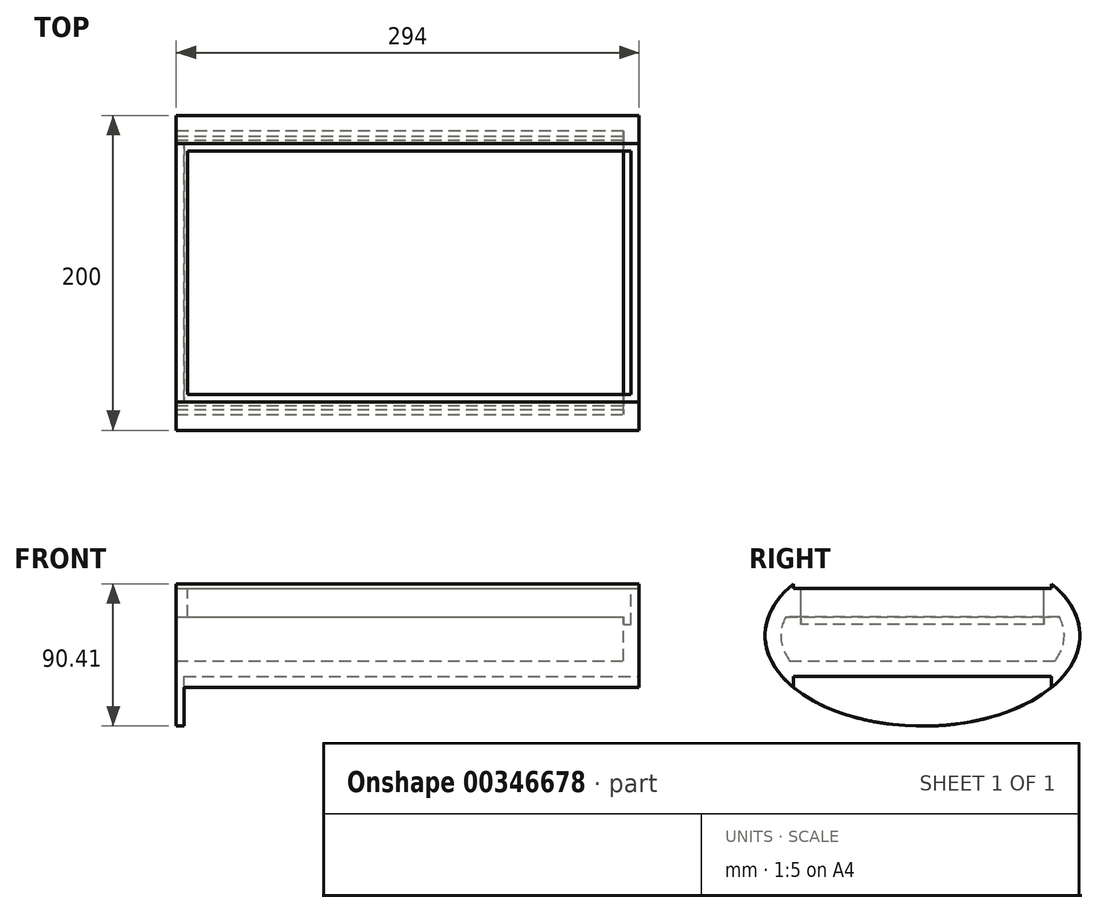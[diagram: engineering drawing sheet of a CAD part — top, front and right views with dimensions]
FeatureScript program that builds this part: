
annotation { "Feature Type Name" : "Feature", "Feature Type Description" : "" }
export const myFeature = defineFeature(function(context is Context, id is Id, definition is map)
    precondition{}
    {
        {
            var Q0;
            Q0=qCreatedBy(makeId("Top.planeOp"),FACE);
            var sketch = newSketch(context, id + "F0", { "sketchPlane" : qUnion([Q0])});
            skLineSegment(sketch, "E0.bottom", {"start": v(-139.7, 76.2) * mm, "end": v(139.7, 76.2) * mm});
            skLineSegment(sketch, "E0.top", {"start": v(-139.7, -76.2) * mm, "end": v(139.7, -76.2) * mm});
            skLineSegment(sketch, "E0.left", {"start": v(-139.7, 76.2) * mm, "end": v(-139.7, -76.2) * mm});
            skLineSegment(sketch, "E0.right", {"start": v(139.7, 76.2) * mm, "end": v(139.7, -76.2) * mm});
            skCircle(sketch, "E1", {"center": v(-9.53, 69.85) * mm, "radius": 3.1 * mm});
            skCircle(sketch, "E2", {"center": v(-6.2, -69.85) * mm, "radius": 3.1 * mm});
            skCircle(sketch, "E3", {"center": v(133.35, -69.85) * mm, "radius": 3.1 * mm});
            skCircle(sketch, "E4", {"center": v(133.35, 0) * mm, "radius": 3.1 * mm});
            skCircle(sketch, "E5", {"center": v(63.5, 0) * mm, "radius": 3.1 * mm});
            skCircle(sketch, "E6", {"center": v(133.35, 69.85) * mm, "radius": 3.1 * mm});
            skPoint(sketch, "E7", {"position": v(0, -76.2) * mm});
            skCircle(sketch, "E8.MirrorC", {"center": v(-133.35, 69.85) * mm, "radius": 3.1 * mm});
            skCircle(sketch, "E9.MirrorC", {"center": v(-133.35, 0) * mm, "radius": 3.1 * mm});
            skCircle(sketch, "E10.MirrorC", {"center": v(-133.35, -69.85) * mm, "radius": 3.1 * mm});
            skCircle(sketch, "E11.MirrorC", {"center": v(-63.5, 0) * mm, "radius": 3.1 * mm});
            skSolve(sketch);
        }
        {
            var Q0;
            Q0=qSketchRegion(id+"F0",true);
            extrude(context, id + "F1", {"entities" : qUnion([Q0]), "depth" : 2 * mm});
        }
        {
            var Q0;
            Q0=makeQuery(id+"F1.opExtrude","CAP_FACE",FACE,{"disambiguationData":[OSD([sQuery(id+"F0.wireOp",EDGE,"E0.bottom"),sQuery(id+"F0.wireOp",EDGE,"E0.top"),sQuery(id+"F0.wireOp",EDGE,"E0.left"),sQuery(id+"F0.wireOp",EDGE,"E0.right"),sQuery(id+"F0.wireOp",EDGE,"E1"),sQuery(id+"F0.wireOp",EDGE,"E2"),sQuery(id+"F0.wireOp",EDGE,"E3"),sQuery(id+"F0.wireOp",EDGE,"E4"),sQuery(id+"F0.wireOp",EDGE,"E5"),sQuery(id+"F0.wireOp",EDGE,"E6"),sQuery(id+"F0.wireOp",EDGE,"E8.MirrorC"),sQuery(id+"F0.wireOp",EDGE,"E9.MirrorC"),sQuery(id+"F0.wireOp",EDGE,"E10.MirrorC"),sQuery(id+"F0.wireOp",EDGE,"E11.MirrorC")])],"isStart":false});
            var sketch = newSketch(context, id + "F2", { "sketchPlane" : qUnion([Q0])});
            skCircle(sketch, "E12", {"center": v(38.1, 25.4) * mm, "radius": 12.7 * mm});
            skCircle(sketch, "E13", {"center": v(88.9, 25.4) * mm, "radius": 12.7 * mm});
            skCircle(sketch, "E14", {"center": v(88.9, -25.4) * mm, "radius": 12.7 * mm});
            skCircle(sketch, "E15", {"center": v(38.1, -25.4) * mm, "radius": 12.7 * mm});
            skCircle(sketch, "E16.MirrorC", {"center": v(-38.1, 25.4) * mm, "radius": 12.7 * mm});
            skCircle(sketch, "E17.MirrorC", {"center": v(-88.9, 25.4) * mm, "radius": 12.7 * mm});
            skCircle(sketch, "E18.MirrorC", {"center": v(-88.9, -25.4) * mm, "radius": 12.7 * mm});
            skCircle(sketch, "E19.MirrorC", {"center": v(-38.1, -25.4) * mm, "radius": 12.7 * mm});
            skSolve(sketch);
        }
        {
            var Q0;
            Q0=makeQuery(id+"F2.imprint","IMPRINT",FACE,{"disambiguationData":[TD([[makeQuery(id+"F2.imprint","IMPRINT",EDGE,{"derivedFrom":sQuery(id+"F2.wireOp",EDGE,"E12")}),-1.0]])]});
            extrude(context, id + "F3", {"entities" : qUnion([Q0]), "operationType" : NewBodyOperationType.REMOVE, "oppositeDirection" : true, "depth" : .1 * mm});
        }
        {
            var Q0;
            Q0=makeQuery(id+"F1.opExtrude","CAP_FACE",FACE,{"disambiguationData":[OSD([sQuery(id+"F0.wireOp",EDGE,"E0.bottom"),sQuery(id+"F0.wireOp",EDGE,"E0.top"),sQuery(id+"F0.wireOp",EDGE,"E0.left"),sQuery(id+"F0.wireOp",EDGE,"E0.right"),sQuery(id+"F0.wireOp",EDGE,"E1"),sQuery(id+"F0.wireOp",EDGE,"E2"),sQuery(id+"F0.wireOp",EDGE,"E3"),sQuery(id+"F0.wireOp",EDGE,"E4"),sQuery(id+"F0.wireOp",EDGE,"E5"),sQuery(id+"F0.wireOp",EDGE,"E6"),sQuery(id+"F0.wireOp",EDGE,"E8.MirrorC"),sQuery(id+"F0.wireOp",EDGE,"E9.MirrorC"),sQuery(id+"F0.wireOp",EDGE,"E10.MirrorC"),sQuery(id+"F0.wireOp",EDGE,"E11.MirrorC")])],"isStart":true});
            var sketch = newSketch(context, id + "F4", { "sketchPlane" : qUnion([Q0])});
            skCircle(sketch, "E20", {"center": v(88.9, 61.12) * mm, "radius": 9.52 * mm});
            skCircle(sketch, "E21", {"center": v(-72.61, 61.12) * mm, "radius": 9.52 * mm});
            skCircle(sketch, "E22", {"center": v(-72.61, -60.83) * mm, "radius": 9.52 * mm});
            skCircle(sketch, "E23", {"center": v(88.9, -60.83) * mm, "radius": 9.52 * mm});
            skSolve(sketch);
        }
        {
            var Q0;
            Q0=qSketchRegion(id+"F4",true);
            extrude(context, id + "F5", {"entities" : qUnion([Q0]), "operationType" : NewBodyOperationType.REMOVE, "oppositeDirection" : true, "depth" : .1 * mm});
        }
        {
            var Q0;
            Q0=qCreatedBy(makeId("Right.planeOp"),FACE);
            cPlane(context, id + "F6", {"entities" : qUnion([Q0]), "cplaneType" : CPlaneType.OFFSET, "offset" : 148 * mm, "oppositeDirection" : true, "width" : 150 * mm, "height" : 150 * mm});
        }
        {
            var Q0;
            Q0=qCreatedBy(makeId("Right.planeOp"),FACE);
            cPlane(context, id + "F7", {"entities" : qUnion([Q0]), "cplaneType" : CPlaneType.OFFSET, "offset" : 146 * mm, "width" : 150 * mm, "height" : 150 * mm});
        }
        {
            var Q0;
            Q0=qCreatedBy(makeId("Top.planeOp"),FACE);
            cPlane(context, id + "F8", {"entities" : qUnion([Q0]), "cplaneType" : CPlaneType.OFFSET, "offset" : 51 * mm, "oppositeDirection" : true, "width" : 150 * mm, "height" : 150 * mm});
        }
        {
            var Q0;
            Q0=qCreatedBy(id+"F6.planeOp",FACE);
            var sketch = newSketch(context, id + "F9", { "sketchPlane" : qUnion([Q0])});
            skEllipse(sketch, "E24", {"center": v(0, -30) * mm, "majorRadius": 100 * mm, "minorRadius": 57.5 * mm, "majorAxis": v(-1, 0)});
            skSolve(sketch);
        }
        {
            var Q0;
            Q0=qCreatedBy(id+"F7.planeOp",FACE);
            var sketch = newSketch(context, id + "F10", { "sketchPlane" : qUnion([Q0])});
            skEllipse(sketch, "E25", {"center": v(0, -30) * mm, "majorRadius": 100 * mm, "minorRadius": 57.5 * mm, "majorAxis": v(1, 0)});
            skSolve(sketch);
        }
        {
            var Q1;
            Q1=makeQuery(id+"F9.imprint","IMPRINT",FACE,{"disambiguationData":[TD([[makeQuery(id+"F9.imprint","IMPRINT",EDGE,{"derivedFrom":sQuery(id+"F9.wireOp",EDGE,"E24")}),1.0]])]});
            var Q2;
            Q2=makeQuery(id+"F10.imprint","IMPRINT",FACE,{"disambiguationData":[TD([[makeQuery(id+"F10.imprint","IMPRINT",EDGE,{"derivedFrom":sQuery(id+"F10.wireOp",EDGE,"E25")}),1.0]])]});
            loft(context, id + "F11", {"sheetProfilesArray" : [{ "sheetProfileEntities" : qUnion([Q1]) }, { "sheetProfileEntities" : qUnion([Q2]) }]});
        }
        {
            var Q0;
            Q0=qCreatedBy(id+"F8.planeOp",FACE);
            cPlane(context, id + "F12", {"entities" : qUnion([Q0]), "cplaneType" : CPlaneType.OFFSET, "offset" : 5 * mm, "oppositeDirection" : true, "width" : 150 * mm, "height" : 150 * mm});
        }
        {
            var Q0;
            Q0=qCreatedBy(id+"F12.planeOp",FACE);
            var sketch = newSketch(context, id + "F13", { "sketchPlane" : qUnion([Q0])});
            skLineSegment(sketch, "E26.bottom", {"start": v(-143, -82) * mm, "end": v(146, -82) * mm});
            skLineSegment(sketch, "E26.top", {"start": v(-143, 82) * mm, "end": v(146, 82) * mm});
            skLineSegment(sketch, "E26.left", {"start": v(-143, -82) * mm, "end": v(-143, 82) * mm});
            skLineSegment(sketch, "E26.right", {"start": v(146, -82) * mm, "end": v(146, 82) * mm});
            skSolve(sketch);
        }
        {
            var Q0;
            Q0=qCreatedBy(makeId("Top.planeOp"),FACE);
            var sketch = newSketch(context, id + "F14", { "sketchPlane" : qUnion([Q0])});
            skLineSegment(sketch, "E27.bottom", {"start": v(-148, 82) * mm, "end": v(146, 82) * mm});
            skLineSegment(sketch, "E27.top", {"start": v(-148, -82) * mm, "end": v(146, -82) * mm});
            skLineSegment(sketch, "E27.left", {"start": v(-148, 82) * mm, "end": v(-148, -82) * mm});
            skLineSegment(sketch, "E27.right", {"start": v(146, 82) * mm, "end": v(146, -82) * mm});
            skSolve(sketch);
        }
        {
            var Q0;
            Q0=qSketchRegion(id+"F14",true);
            extrude(context, id + "F15", {"entities" : qUnion([Q0]), "operationType" : NewBodyOperationType.REMOVE, "depth" : 32 * mm});
        }
        {
            var Q0;
            Q0=makeQuery(id+"F13.imprint","IMPRINT",FACE,{"disambiguationData":[TD([[makeQuery(id+"F13.imprint","IMPRINT",EDGE,{"derivedFrom":sQuery(id+"F13.wireOp",EDGE,"E26.bottom")}),1.0]])]});
            extrude(context, id + "F16", {"entities" : qUnion([Q0]), "operationType" : NewBodyOperationType.REMOVE, "oppositeDirection" : true, "depth" : 40 * mm});
        }
        {
            var Q0;
            Q0=makeQuery(id+"F2.imprint","IMPRINT",FACE,{"disambiguationData":[TD([[makeQuery(id+"F2.imprint","IMPRINT",EDGE,{"derivedFrom":sQuery(id+"F2.wireOp",EDGE,"E12")}),-1.0]])]});
            var sketch = newSketch(context, id + "F17", { "sketchPlane" : qUnion([Q0])});
            skLineSegment(sketch, "E28.bottom", {"start": v(-140.7, 77.2) * mm, "end": v(140.7, 77.2) * mm});
            skLineSegment(sketch, "E28.top", {"start": v(-140.7, -77.2) * mm, "end": v(140.7, -77.2) * mm});
            skLineSegment(sketch, "E28.left", {"start": v(-140.7, 77.2) * mm, "end": v(-140.7, -77.2) * mm});
            skLineSegment(sketch, "E28.right", {"start": v(140.7, 77.2) * mm, "end": v(140.7, -77.2) * mm});
            skSolve(sketch);
        }
        {
            var Q0;
            Q0=qSketchRegion(id+"F17",true);
            extrude(context, id + "F18", {"entities" : qUnion([Q0]), "operationType" : NewBodyOperationType.REMOVE, "oppositeDirection" : true, "depth" : 10 * mm});
        }
        {
            var Q0;
            Q0=makeQuery(id+"F11.opLoft","CAP_FACE",FACE,{"disambiguationData":[OSD([makeQuery(id+"F9.imprint","IMPRINT",FACE,{"disambiguationData":[TD([[makeQuery(id+"F9.imprint","IMPRINT",EDGE,{"derivedFrom":sQuery(id+"F9.wireOp",EDGE,"E24")}),1.0]])]})])],"isStart":true});
            var Q1;
            Q1=makeQuery(id+"F11.opLoft","CAP_FACE",FACE,{"disambiguationData":[OSD([makeQuery(id+"F10.imprint","IMPRINT",FACE,{"disambiguationData":[TD([[makeQuery(id+"F10.imprint","IMPRINT",EDGE,{"derivedFrom":sQuery(id+"F10.wireOp",EDGE,"E25")}),1.0]])]})])],"isStart":true});
            shell(context, id + "F19", {"entities" : qUnion([Q0, Q1]), "thickness" : 10 * mm});
        }
        {
            var Q0;
            Q0=qSketchRegion(id+"F17",true);
            extrude(context, id + "F20", {"entities" : qUnion([Q0]), "operationType" : NewBodyOperationType.REMOVE, "oppositeDirection" : true, "depth" : 25 * mm});
        }
    });
